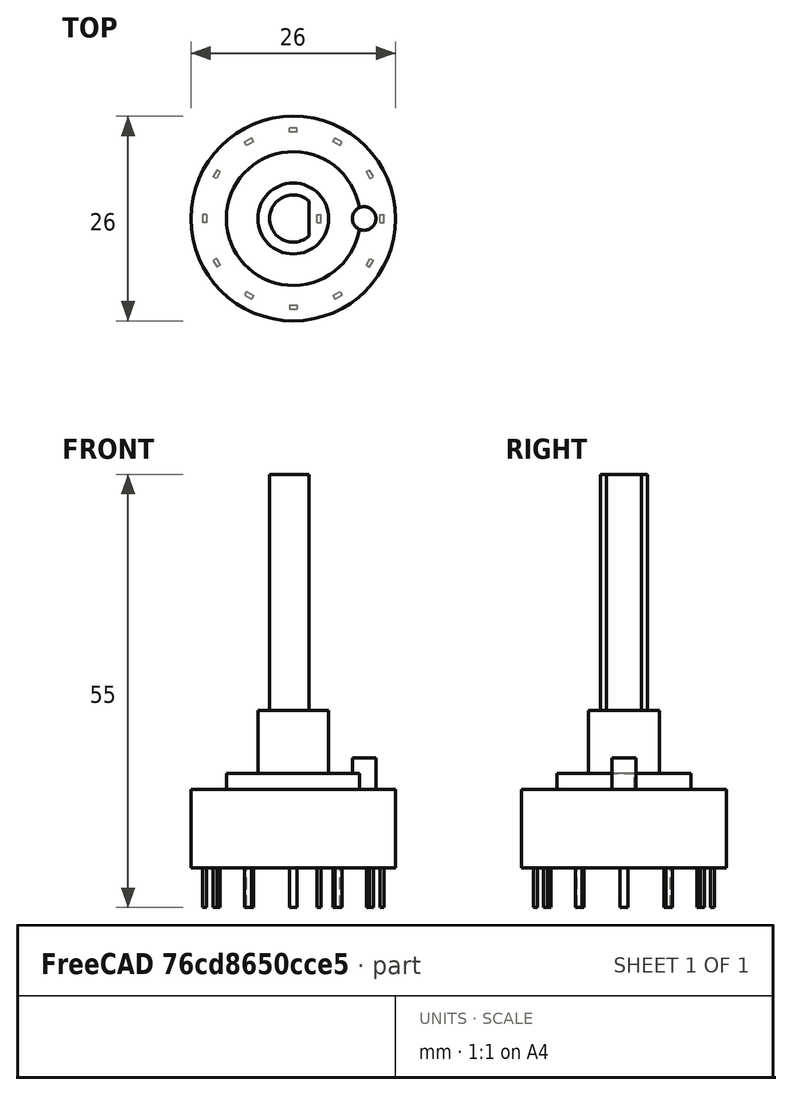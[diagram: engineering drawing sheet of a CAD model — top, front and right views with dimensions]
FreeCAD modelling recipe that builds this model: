
FCSTD DOCUMENT  (FreeCAD 0.17R13541 (Git))
Label: rotary selector
License: All rights reserved
LicenseURL: http://en.wikipedia.org/wiki/All_rights_reserved
objects: Part::Cylinder×5, Part::Box×3, Part::FeaturePython×1, Part::Cut×1, Part::MultiFuse×1
note: 11 computed .brp shape members not serialized (recipe doc carries the construction recipe); baked Part::Feature solids carry a one-line shape summary decoded from their .brp

FEATURE [Part::Cylinder] Cylinder  label="Cuerpo 1"
  Angle = 360
  AttacherType = Attacher::AttachEngine3D
  Height = 10
  Radius = 13
FEATURE [Part::Cylinder] Cylinder001  label="Cuerpo 2"
  Angle = 360
  AttacherType = Attacher::AttachEngine3D
  Height = 2
  Placement = pos=(0,0,10) rot=(0,0,1;0rad)
  Radius = 8.5
FEATURE [Part::Box] Box  label="Pin"
  AttacherType = Attacher::AttachEngine3D
  Height = 5
  Length = 0.5
  Placement = pos=(11,-0.5,-5) rot=(0,0,1;0rad)
  Width = 1
FEATURE [Part::FeaturePython] Array  label="Pin array"  # Draft array (typed FeaturePython)
  Angle = 360
  ArrayType = 1
  Axis = (0,0,1)
  Base = -> Box
  Center = (0,0,0)
  Fuse = false
  IntervalAxis = (0,0,0)
  IntervalX = (1,0,0)
  IntervalY = (0,1,0)
  IntervalZ = (0,0,0)
  NumberPolar = 12
  NumberX = 2
  NumberY = 2
  NumberZ = 1
FEATURE [Part::Box] Box001  label="Pin central"
  AttacherType = Attacher::AttachEngine3D
  Height = 5
  Length = 0.5
  Placement = pos=(3,-0.5,-5) rot=(0,0,1;0rad)
  Width = 1
FEATURE [Part::Cylinder] Cylinder002  label="Cuerpo 3"
  Angle = 360
  AttacherType = Attacher::AttachEngine3D
  Height = 8
  Placement = pos=(0,0,12) rot=(0,0,1;0rad)
  Radius = 4.5
FEATURE [Part::Cylinder] Cylinder003  label="Cuerpo 4"
  Angle = 360
  AttacherType = Attacher::AttachEngine3D
  Height = 30
  Placement = pos=(0,0,20) rot=(0,0,1;0rad)
  Radius = 3
FEATURE [Part::Cylinder] Cylinder004  label="Cuerpo 5"
  Angle = 360
  AttacherType = Attacher::AttachEngine3D
  Height = 4
  Placement = pos=(9,0,10) rot=(0,0,1;0rad)
  Radius = 1.5
FEATURE [Part::Box] Box002  label="Recorte"
  AttacherType = Attacher::AttachEngine3D
  Height = 30
  Length = 1
  Placement = pos=(2,-5,20) rot=(0,0,1;0rad)
  Width = 10
FEATURE [Part::Cut] Cut  label="Cuerpo 4 recortado"
  Base = -> Cylinder003
  Refine = true
  Tool = -> Box002
FEATURE [Part::MultiFuse] Fusion  label="Selector final"
  Refine = true
  Shapes = -> [Cylinder,Cylinder001,Array,Box001,Cylinder002,Cylinder004,Cut]
